# Revit family: PRD_FrankeWS_WlHngWshBsns_AnimaWashbasin_WT450,LP20
name_source: partatom
category: Plumbing Fixtures
revit_build: Autodesk Revit 2018 (Build: 20190510_1515(x64)
units: mm (PartAtom-declared; Revit-internal decimal feet)

## family parameters
Cut with Voids When Loaded = No
Host = Face
OmniClass Number = 23.45.05.14.14
OmniClass Title = Sinks/Lavatories
Part Type = Normal
Room Calculation Point = No
Round Connector Dimension = Use Diameter
Shared = No

## types (2) — shared parameters
AssetType = Fixed
Category = Pr_40_20_96_96, Wall-hung wash basins
Color = Stainless steel
Default Elevation = 850 mm  [stored 2.78871 ft]
DrainSize = DN 32 (1 1/4 inch.)
DurationUnit = year
Finish = Satin finished
Flow = 0.0 L/s
Form = Wall hung wash basin
IfcExportAs = IfcSanitaryTerminalType
IfcExportType = WASHHANDBASIN
IntegralAccessories = Incl. stainless steel screws and dowels
Manufacturer = KWC Group AG
ManufacturerName = KWC Group AG
ManufacturerURL = www.kwc.com
Material = Stainless steel
MaterialCode = Stainless steel 1.4301
NBSDescription = Wall hung wash basins
NBSReference = 45-35-70/369
NominalDepth = 450 mm  [stored 1.47638 ft]
NominalWidth = 450 mm  [stored 1.47638 ft]
OutletSize = DN 32 (1 1/4 inch.)
ProductInformation = https://pim.kwc.com
Shape = Rectangular
SinkMaterial = PRD_AR_StainlessSteel_SatinFinished
SinkMounting = WallHung
SinkType = HandRinse
SplashbackMaterial = PRD_AR_StainlessSteel_SatinFinished
TapLedge = no
TypeOfMounting = Wall mounting
URL = www.kwc.com
Uniclass2015Code = Pr_40_20_96_96
Uniclass2015Title = Wall-hung wash basins
Uniclass2015Version = Products v1.10
Version = 1
WarrantyDurationUnit = year
WashbasinMaterial = PRD_AR_StainlessSteel_SatinFinished
WasteSize = 32  [stored 0.104987 ft]

## per-type parameters (varying)
| type | BIMObjectName | Description | Features | GrossWeight | LP20Tap | ModelNumber | Name | NetWeight | NominalHeight | Overflow | OverflowLocation | Size | TypeOfWasteKit | WasteHolePosition |
| WT450 | PRD_AR_WallHungWashBasins_AnimaWashbasin_WT450 | Single wash basin, stainless steel, material thickness 0,9 mm, surface satin finished, circular bowl with diameter 380 mm, rear upstand, single tap hole, 32 mm waste/overflow fitting, Incl. screws and dowels. Tap hole right. | stainless steel, 0,90 mm, satin finished, wall mounting, 450x205x450 mm (WxHxD) | 6.60 kg | No | 2000100365 | ANIMA wall-hung wash basin WT450 | 5.50 kg | 205 mm  [stored 0.672572 ft] | yes | back | 450 x 450 x 205 mm | Plug waste | Centre-centre |
| LP20 | PRD_AR_WallHungWashBasins_AnimaWashbasin_LP20 | Single wash basin for wall mounting, stainless steel, surface satin finished, material thickness 1 mm, seamless welded round sink with diameter 385 mm, 35 mm tap ledge, without overflow, 1 1/4" plug waste, waste centric, incl. preassembled water spout, 200 mm high front panel with included self-closing valve for knee- or hip operations, watertemperature adjustable, incl. screws and dowels | stainless steel, 1,00 mm, satin finished, wall mounting, 450x175x450 mm (WxHxD) | 6.80 kg | Yes | 2000100059 | Anima wall-hung wash basins LP20 | 5.80 kg | 175 mm  [stored 0.574147 ft] | no |  | 450 x 450 x 175 mm | perforated waste | Center |

note: column(s) folded — value = type name in every type: Model, ModelReference, Type

note: [stored X ft] marks values corroborated as IEEE doubles in the binary element streams (Revit-internal decimal feet)

## geometry (parser evidence)
native form markers: Sweep x14
no freeform markers — native parametric forms only
